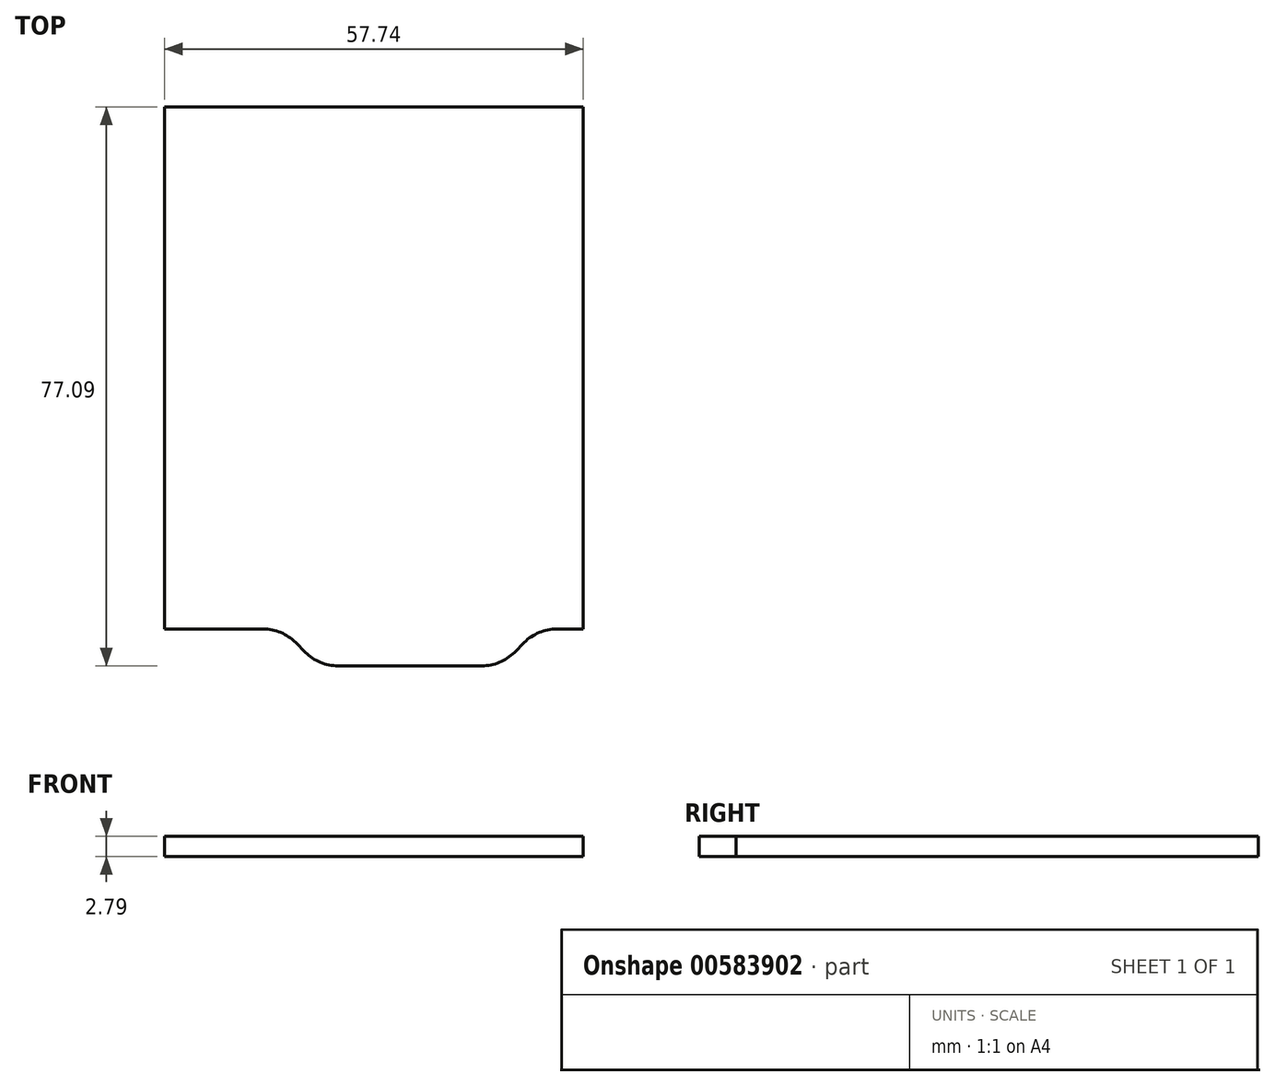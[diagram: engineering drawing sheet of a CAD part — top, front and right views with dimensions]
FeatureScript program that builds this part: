
annotation { "Feature Type Name" : "Feature", "Feature Type Description" : "" }
export const myFeature = defineFeature(function(context is Context, id is Id, definition is map)
    precondition{}
    {
        {
            var Q0;
            Q0=qCreatedBy(makeId("Top.planeOp"),FACE);
            var sketch = newSketch(context, id + "F0", { "sketchPlane" : qUnion([Q0])});
            skLineSegment(sketch, "E0", {"start": v(-28.87, 48.13) * mm, "end": v(28.87, 48.13) * mm});
            skLineSegment(sketch, "E1", {"start": v(28.87, 48.13) * mm, "end": v(28.87, -23.88) * mm});
            skLineSegment(sketch, "E2", {"start": v(28.87, -23.88) * mm, "end": v(25.25, -23.88) * mm});
            skLineSegment(sketch, "E3", {"start": v(20.76, -25.74) * mm, "end": v(19.4, -27.1) * mm});
            skLineSegment(sketch, "E4", {"start": v(14.9, -28.96) * mm, "end": v(-4.92, -28.96) * mm});
            skLineSegment(sketch, "E5", {"start": v(-9.4, -27.1) * mm, "end": v(-10.77, -25.74) * mm});
            skLineSegment(sketch, "E6", {"start": v(-15.26, -23.88) * mm, "end": v(-28.87, -23.88) * mm});
            skLineSegment(sketch, "E7", {"start": v(-28.87, -23.88) * mm, "end": v(-28.87, 48.13) * mm});
            skPoint(sketch, "E8.visualSharp", {"position": v(-12.63, -23.88) * mm});
            skArc(sketch, "E8.filletArc", {"start": v(-10.77, -25.74) * mm, "mid": v(-12.83, -24.36) * mm, "end": v(-15.26, -23.88) * mm});
            skPoint(sketch, "E9.visualSharp", {"position": v(-7.55, -28.96) * mm});
            skArc(sketch, "E9.filletArc", {"start": v(-9.4, -27.1) * mm, "mid": v(-7.35, -28.47) * mm, "end": v(-4.92, -28.96) * mm});
            skPoint(sketch, "E10.visualSharp", {"position": v(17.54, -28.96) * mm});
            skArc(sketch, "E10.filletArc", {"start": v(14.9, -28.96) * mm, "mid": v(17.34, -28.47) * mm, "end": v(19.4, -27.1) * mm});
            skPoint(sketch, "E11.visualSharp", {"position": v(22.62, -23.88) * mm});
            skArc(sketch, "E11.filletArc", {"start": v(25.25, -23.88) * mm, "mid": v(22.82, -24.36) * mm, "end": v(20.76, -25.74) * mm});
            skSolve(sketch);
        }
        {
            var Q0;
            Q0=makeQuery(id+"F0.imprint","IMPRINT",FACE,{"disambiguationData":[TD([[makeQuery(id+"F0.imprint","IMPRINT",EDGE,{"derivedFrom":sQuery(id+"F0.wireOp",EDGE,"E0")}),-1.0]])]});
            extrude(context, id + "F1", {"entities" : qUnion([Q0]), "depth" : 2.8 * mm, "offsetDistance" : 25.4 * mm});
        }
    });
